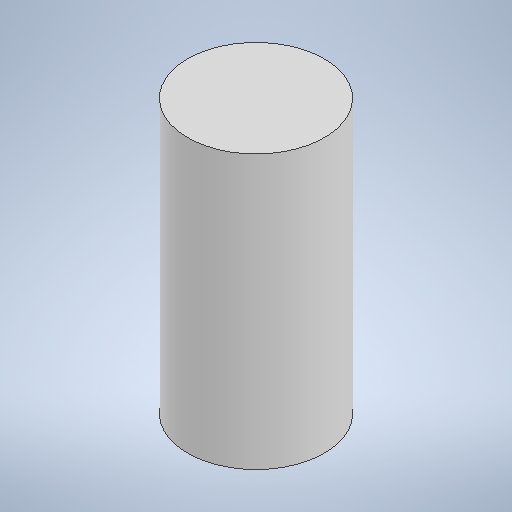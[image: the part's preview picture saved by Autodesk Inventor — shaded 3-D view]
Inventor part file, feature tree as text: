
AUTODESK INVENTOR PART (.ipt)
format: ipt  version: 2025.2 (Build 292293000, 293)  size: 205,824 bytes
history: native  units: mm
features: extrude x1, sketch x1
ambient origin geometry x8: Origin, YZ Plane, XZ Plane, XY Plane, X Axis, Y Axis, Z Axis, Center Point
bodies: Solid1 (feature_tree)
feature tree (2):
  extrude  "Extrusion1"  Depth=6.0mm TaperAngle=0.0deg
  sketch  "Sketch1"  dims[d0=3.0mm d1=6.0mm d2=0.0mm]
